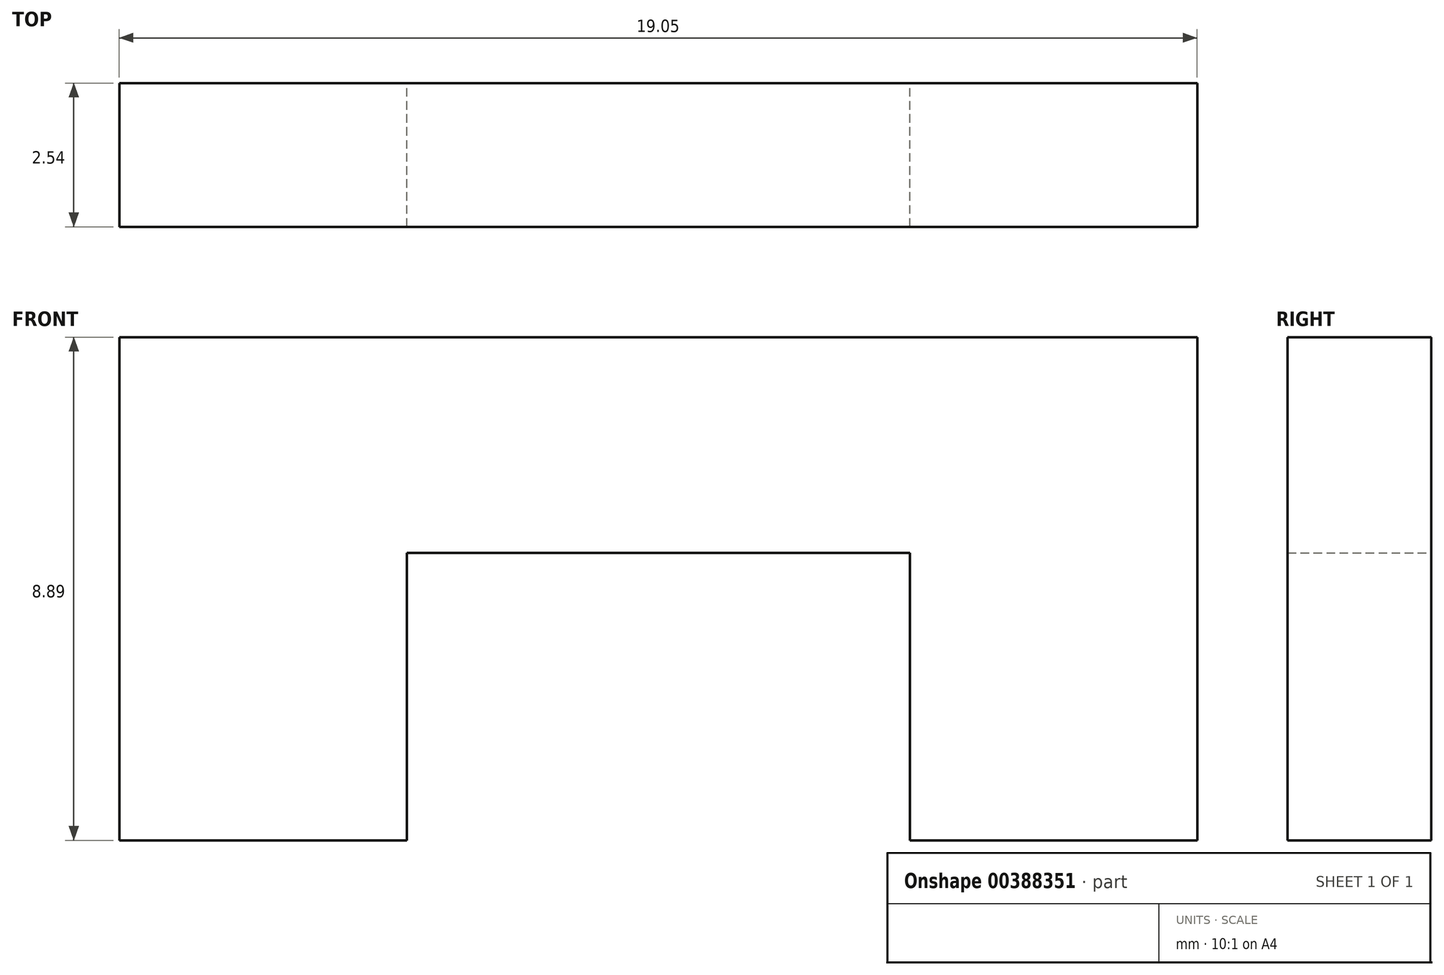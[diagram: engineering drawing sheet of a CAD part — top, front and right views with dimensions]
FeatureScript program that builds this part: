
annotation { "Feature Type Name" : "Feature", "Feature Type Description" : "" }
export const myFeature = defineFeature(function(context is Context, id is Id, definition is map)
    precondition{}
    {
        {
            var Q0;
            Q0=qCreatedBy(makeId("Front.planeOp"),FACE);
            var sketch = newSketch(context, id + "F0", { "sketchPlane" : qUnion([Q0])});
            skLineSegment(sketch, "E0", {"start": v(-54.84, -24.73) * mm, "end": v(-54.84, -15.84) * mm});
            skLineSegment(sketch, "E1", {"start": v(-54.84, -15.84) * mm, "end": v(-35.79, -15.84) * mm});
            skLineSegment(sketch, "E2", {"start": v(-35.79, -15.84) * mm, "end": v(-35.79, -24.73) * mm});
            skLineSegment(sketch, "E3", {"start": v(-54.84, -24.73) * mm, "end": v(-49.76, -24.73) * mm});
            skLineSegment(sketch, "E4", {"start": v(-35.79, -24.73) * mm, "end": v(-40.87, -24.73) * mm});
            skLineSegment(sketch, "E5", {"start": v(-49.76, -24.73) * mm, "end": v(-49.76, -19.65) * mm});
            skLineSegment(sketch, "E6", {"start": v(-40.87, -24.73) * mm, "end": v(-40.87, -19.65) * mm});
            skLineSegment(sketch, "E7", {"start": v(-49.76, -19.65) * mm, "end": v(-40.87, -19.65) * mm});
            skSolve(sketch);
        }
        {
            var Q0;
            Q0=makeQuery(id+"F0.imprint","IMPRINT",FACE,{"disambiguationData":[TD([[makeQuery(id+"F0.imprint","IMPRINT",EDGE,{"derivedFrom":sQuery(id+"F0.wireOp",EDGE,"E0")}),-1.0]])]});
            extrude(context, id + "F1", {"entities" : qUnion([Q0]), "depth" : 2.54 * mm});
        }
    });
